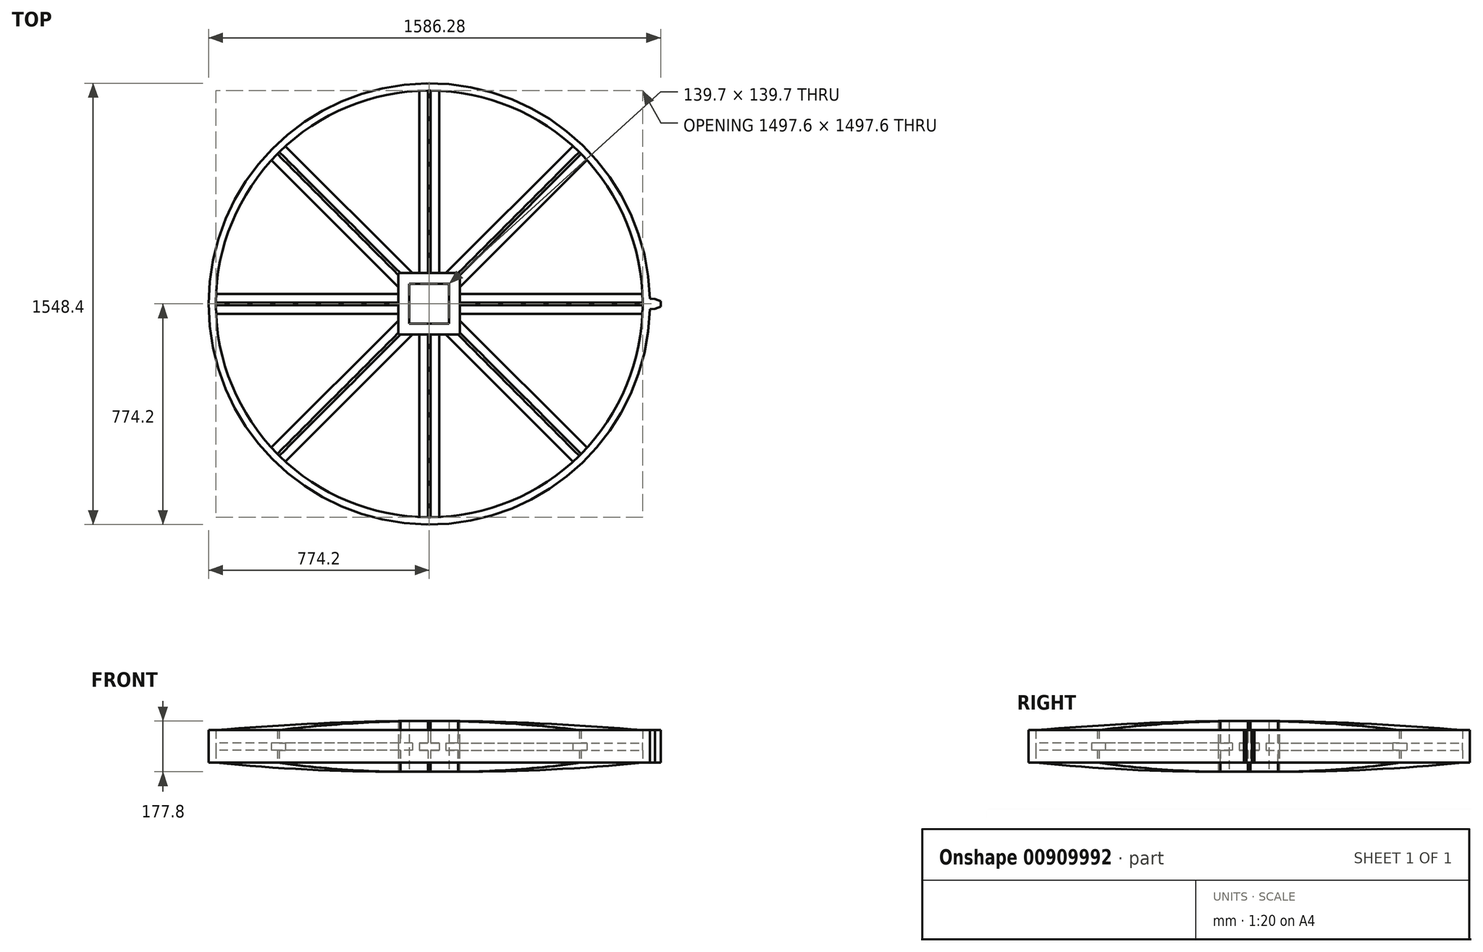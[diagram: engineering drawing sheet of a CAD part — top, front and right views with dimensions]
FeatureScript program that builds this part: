
annotation { "Feature Type Name" : "Feature", "Feature Type Description" : "" }
export const myFeature = defineFeature(function(context is Context, id is Id, definition is map)
    precondition{}
    {
        {
            var Q0;
            Q0=qCreatedBy(makeId("Front.planeOp"),FACE);
            var sketch = newSketch(context, id + "F0", { "sketchPlane" : qUnion([Q0])});
            skLineSegment(sketch, "E0.bottom", {"start": v(0, -88.9) * mm, "end": v(107.95, -88.9) * mm});
            skLineSegment(sketch, "E0.top", {"start": v(0, 88.9) * mm, "end": v(107.95, 88.9) * mm});
            skLineSegment(sketch, "E0.left", {"start": v(0, -88.9) * mm, "end": v(0, 88.9) * mm});
            skLineSegment(sketch, "E0.right", {"start": v(107.95, -88.9) * mm, "end": v(107.95, 88.9) * mm});
            skLineSegment(sketch, "E1.bottom", {"start": v(748.8, -57.15) * mm, "end": v(774.2, -57.15) * mm});
            skLineSegment(sketch, "E1.top", {"start": v(748.8, 57.15) * mm, "end": v(774.2, 57.15) * mm});
            skLineSegment(sketch, "E1.left", {"start": v(748.8, -57.15) * mm, "end": v(748.8, 57.15) * mm});
            skLineSegment(sketch, "E1.right", {"start": v(774.2, -57.15) * mm, "end": v(774.2, 57.15) * mm});
            skLineSegment(sketch, "E2", {"start": v(82.55, 88.9) * mm, "end": v(82.55, -88.9) * mm});
            skLineSegment(sketch, "E3", {"start": v(82.55, 12.5) * mm, "end": v(748.8, 12.5) * mm});
            skLineSegment(sketch, "E4", {"start": v(82.55, -12.9) * mm, "end": v(748.8, -12.9) * mm});
            skLineSegment(sketch, "E5", {"start": v(0, -88.9) * mm, "end": v(0, -224.91) * mm, "construction": true});
            skArc(sketch, "E6", {"start": v(748.8, 57.15) * mm, "mid": v(428.67, 78.96) * mm, "end": v(107.95, 88.9) * mm});
            skPoint(sketch, "E7", {"position": v(0, 0) * mm});
            skLineSegment(sketch, "E8", {"start": v(748.8, 0) * mm, "end": v(0, 0) * mm, "construction": true});
            skArc(sketch, "E9", {"start": v(107.95, -88.9) * mm, "mid": v(428.77, -80.96) * mm, "end": v(748.8, -57.15) * mm});
            skSolve(sketch);
        }
        {
            var Q0;
            {var subQ0=sQuery(id+"F0.wireOp",EDGE,"E0.left");Q0=makeQuery(id+"F0.imprint","IMPRINT",FACE,{"disambiguationData":[TD([[makeQuery(id+"F0.imprint","IMPRINT",EDGE,{"derivedFrom":subQ0}),-1.0]])]});}
            var Q1;
            {var subQ6=sQuery(id+"F0.wireOp",EDGE,"E2");Q1=makeQuery(id+"F0.imprint","IMPRINT",FACE,{"disambiguationData":[TD([[makeQuery(id+"F0.imprint","IMPRINT",EDGE,{"derivedFrom":subQ6}),1.0]])]});}
            var Q2;
            Q2=sQuery(id+"F0.wireOp",EDGE,"E0.left");
            revolve(context, id + "F1", {"surfaceOperationType" : NewSurfaceOperationType.NEW, "entities" : qUnion([Q0, Q1]), "axis" : qUnion([Q2]), "revolveType" : RevolveType.SYMMETRIC, "angle" : 45 * degree});
        }
        {
            var Q0;
            {var subQ0=sQuery(id+"F0.wireOp",EDGE,"E4");var subQ1=sQuery(id+"F0.wireOp",EDGE,"E0.right");var subQ2=makeQuery(id+"F0.imprint","INTERSECT",VERTEX,{"derivedFrom":[subQ1,subQ0]});Q0=makeQuery(id+"F0.imprint","IMPRINT",FACE,{"disambiguationData":[TD([[makeQuery(id+"F0.imprint","IMPRINT",EDGE,{"disambiguationData":[TD([[subQ2,-1.0]])],"derivedFrom":subQ1}),-1.0]])]});}
            var Q1;
            {var subQ0=sQuery(id+"F0.wireOp",EDGE,"E4");var subQ1=sQuery(id+"F0.wireOp",EDGE,"E0.right");var subQ2=makeQuery(id+"F0.imprint","INTERSECT",VERTEX,{"derivedFrom":[subQ1,subQ0]});Q1=makeQuery(id+"F0.imprint","IMPRINT",FACE,{"disambiguationData":[TD([[makeQuery(id+"F0.imprint","IMPRINT",EDGE,{"disambiguationData":[TD([[subQ2,-1.0]])],"derivedFrom":subQ1}),1.0]])]});}
            extrude(context, id + "F2", {"entities" : qUnion([Q0, Q1]), "operationType" : NewBodyOperationType.ADD, "depth" : 69.85 * mm, "offsetDistance" : 25 * mm, "symmetric" : true});
        }
        {
            var Q0;
            {var subQ3=sQuery(id+"F0.wireOp",EDGE,"E1.bottom");Q0=makeQuery(id+"F0.imprint","IMPRINT",FACE,{"disambiguationData":[TD([[makeQuery(id+"F0.imprint","IMPRINT",EDGE,{"derivedFrom":subQ3}),1.0]])]});}
            var Q1;
            Q1=sQuery(id+"F0.wireOp",EDGE,"E0.left");
            revolve(context, id + "F3", {"operationType" : NewBodyOperationType.ADD, "surfaceOperationType" : NewSurfaceOperationType.NEW, "entities" : qUnion([Q0]), "axis" : qUnion([Q1]), "revolveType" : RevolveType.SYMMETRIC, "angle" : 45 * degree});
        }
        {
            var Q0;
            {var subQ1=sQuery(id+"F0.wireOp",EDGE,"E0.top");var subQ3=sQuery(id+"F0.wireOp",EDGE,"E2");var subQ4=makeQuery(id+"F0.imprint","INTERSECT",VERTEX,{"derivedFrom":[subQ1,subQ3]});Q0=makeQuery(id+"F0.imprint","IMPRINT",FACE,{"disambiguationData":[TD([[makeQuery(id+"F0.imprint","IMPRINT",EDGE,{"disambiguationData":[TD([[subQ4,-1.0]])],"derivedFrom":subQ3}),1.0]])]});}
            var Q1;
            {var subQ1=sQuery(id+"F0.wireOp",EDGE,"E0.bottom");var subQ3=sQuery(id+"F0.wireOp",EDGE,"E2");var subQ4=makeQuery(id+"F0.imprint","INTERSECT",VERTEX,{"derivedFrom":[subQ1,subQ3]});Q1=makeQuery(id+"F0.imprint","IMPRINT",FACE,{"disambiguationData":[TD([[makeQuery(id+"F0.imprint","IMPRINT",EDGE,{"disambiguationData":[TD([[subQ4,1.0]])],"derivedFrom":subQ3}),1.0]])]});}
            var Q2;
            {var subQ0=sQuery(id+"F0.wireOp",EDGE,"E6");Q2=makeQuery(id+"F0.imprint","IMPRINT",FACE,{"disambiguationData":[TD([[makeQuery(id+"F0.imprint","IMPRINT",EDGE,{"derivedFrom":subQ0}),1.0]])]});}
            var Q3;
            {var subQ0=sQuery(id+"F0.wireOp",EDGE,"E9");Q3=makeQuery(id+"F0.imprint","IMPRINT",FACE,{"disambiguationData":[TD([[makeQuery(id+"F0.imprint","IMPRINT",EDGE,{"derivedFrom":subQ0}),1.0]])]});}
            extrude(context, id + "F4", {"entities" : qUnion([Q0, Q1, Q2, Q3]), "operationType" : NewBodyOperationType.ADD, "depth" : 9.53 * mm, "offsetDistance" : 25 * mm, "symmetric" : true});
        }
        {
            var Q0;
            Q0=makeQuery(id+"F1.opRevolve","SWEPT_BODY",BODY,{"disambiguationData":[OSD([sQuery(id+"F0.wireOp",EDGE,"E0.bottom"),sQuery(id+"F0.wireOp",EDGE,"E0.top"),sQuery(id+"F0.wireOp",EDGE,"E0.left"),sQuery(id+"F0.wireOp",EDGE,"E0.right")])]});
            var Q1;
            Q1=sQuery(id+"F0.wireOp",EDGE,"E0.left");
            circularPattern(context, id + "F5", {"operationType" : NewBodyOperationType.ADD, "entities" : qUnion([Q0]), "axis" : qUnion([Q1]), "angle" : 360 * degree, "instanceCount" : 8, "equalSpace" : true});
        }
        {
            var Q0;
            {var subQ0=makeQuery(id+"F3.opRevolve","SWEPT_FACE",FACE,{"disambiguationData":[OSD([sQuery(id+"F0.wireOp",EDGE,"E1.top")])]});Q0=makeQuery(id+"F5.boolean.opBoolean","MERGE",FACE,{"derivedFrom":[subQ0,makeQuery(id+"F5.opPattern","COPY",FACE,{"derivedFrom":subQ0,"instanceName":"1"}),makeQuery(id+"F5.opPattern","COPY",FACE,{"derivedFrom":subQ0,"instanceName":"2"}),makeQuery(id+"F5.opPattern","COPY",FACE,{"derivedFrom":subQ0,"instanceName":"3"}),makeQuery(id+"F5.opPattern","COPY",FACE,{"derivedFrom":subQ0,"instanceName":"4"}),makeQuery(id+"F5.opPattern","COPY",FACE,{"derivedFrom":subQ0,"instanceName":"5"}),makeQuery(id+"F5.opPattern","COPY",FACE,{"derivedFrom":subQ0,"instanceName":"6"}),makeQuery(id+"F5.opPattern","COPY",FACE,{"derivedFrom":subQ0,"instanceName":"7"})]});}
            var sketch = newSketch(context, id + "F6", { "sketchPlane" : qUnion([Q0])});
            skLineSegment(sketch, "E10", {"start": v(773.98, 18.26) * mm, "end": v(792.56, 16.63) * mm});
            skLineSegment(sketch, "E11", {"start": v(792.56, 16.63) * mm, "end": v(812.08, 9.53) * mm});
            skLineSegment(sketch, "E12", {"start": v(812.08, 9.53) * mm, "end": v(812.08, -9.53) * mm});
            skLineSegment(sketch, "E13", {"start": v(812.08, -9.53) * mm, "end": v(792.56, -16.63) * mm});
            skLineSegment(sketch, "E14", {"start": v(792.56, -16.63) * mm, "end": v(773.98, -18.26) * mm});
            skLineSegment(sketch, "E15", {"start": v(0, 0) * mm, "end": v(812.08, 0) * mm, "construction": true});
            skLineSegment(sketch, "E16", {"start": v(773.98, 18.26) * mm, "end": v(773.98, -18.26) * mm});
            skSolve(sketch);
        }
        {
            var Q0;
            {var subQ0=sQuery(id+"F6.wireOp",EDGE,"E10");Q0=makeQuery(id+"F6.imprint","IMPRINT",FACE,{"disambiguationData":[TD([[makeQuery(id+"F6.imprint","IMPRINT",EDGE,{"derivedFrom":subQ0}),-1.0]])]});}
            var Q1;
            {var subQ0=sQuery(id+"F0.wireOp",EDGE,"E0.bottom");var subQ1=makeQuery(id+"F4.boolean.opBoolean","MERGE",FACE,{"derivedFrom":[makeQuery(id+"F1.opRevolve","SWEPT_FACE",FACE,{"disambiguationData":[OSD([subQ0])]}),makeQuery(id+"F3.opRevolve","SWEPT_FACE",FACE,{"disambiguationData":[OSD([sQuery(id+"F0.wireOp",EDGE,"E1.bottom")])]}),makeQuery(id+"F4.opExtrude","SWEPT_FACE",FACE,{"disambiguationData":[OSD([subQ0,sQuery(id+"F0.wireOp",EDGE,"D5k9asr0-8ta1-f4uu-XxQ3-tXAVFih4KlHv")])]})]});Q1=makeQuery(id+"F5.boolean.opBoolean","MERGE",FACE,{"derivedFrom":[subQ1,makeQuery(id+"F5.opPattern","COPY",FACE,{"derivedFrom":subQ1,"instanceName":"1"}),makeQuery(id+"F5.opPattern","COPY",FACE,{"derivedFrom":subQ1,"instanceName":"2"}),makeQuery(id+"F5.opPattern","COPY",FACE,{"derivedFrom":subQ1,"instanceName":"3"}),makeQuery(id+"F5.opPattern","COPY",FACE,{"derivedFrom":subQ1,"instanceName":"4"}),makeQuery(id+"F5.opPattern","COPY",FACE,{"derivedFrom":subQ1,"instanceName":"5"}),makeQuery(id+"F5.opPattern","COPY",FACE,{"derivedFrom":subQ1,"instanceName":"6"}),makeQuery(id+"F5.opPattern","COPY",FACE,{"derivedFrom":subQ1,"instanceName":"7"})]});}
            extrude(context, id + "F7", {"entities" : qUnion([Q0]), "operationType" : NewBodyOperationType.ADD, "oppositeDirection" : true, "depth" : 114.3 * mm, "endBoundEntityFace" : qUnion([Q1]), "offsetDistance" : 25 * mm});
        }
        {
            var Q0;
            {var subQ0=sQuery(id+"F0.wireOp",EDGE,"E0.bottom");var subQ1=makeQuery(id+"F4.boolean.opBoolean","MERGE",FACE,{"derivedFrom":[makeQuery(id+"F1.opRevolve","SWEPT_FACE",FACE,{"disambiguationData":[OSD([subQ0])]}),makeQuery(id+"F3.opRevolve","SWEPT_FACE",FACE,{"disambiguationData":[OSD([sQuery(id+"F0.wireOp",EDGE,"E1.bottom")])]}),makeQuery(id+"F4.opExtrude","SWEPT_FACE",FACE,{"disambiguationData":[OSD([subQ0,sQuery(id+"F0.wireOp",EDGE,"D5k9asr0-8ta1-f4uu-XxQ3-tXAVFih4KlHv")])]})]});Q0=makeQuery(id+"F5.boolean.opBoolean","MERGE",FACE,{"derivedFrom":[subQ1,makeQuery(id+"F5.opPattern","COPY",FACE,{"derivedFrom":subQ1,"instanceName":"1"}),makeQuery(id+"F5.opPattern","COPY",FACE,{"derivedFrom":subQ1,"instanceName":"2"}),makeQuery(id+"F5.opPattern","COPY",FACE,{"derivedFrom":subQ1,"instanceName":"3"}),makeQuery(id+"F5.opPattern","COPY",FACE,{"derivedFrom":subQ1,"instanceName":"4"}),makeQuery(id+"F5.opPattern","COPY",FACE,{"derivedFrom":subQ1,"instanceName":"5"}),makeQuery(id+"F5.opPattern","COPY",FACE,{"derivedFrom":subQ1,"instanceName":"6"}),makeQuery(id+"F5.opPattern","COPY",FACE,{"derivedFrom":subQ1,"instanceName":"7"})]});}
            var sketch = newSketch(context, id + "F8", { "sketchPlane" : qUnion([Q0])});
            skLineSegment(sketch, "E17.bottom", {"start": v(-69.85, 69.85) * mm, "end": v(69.85, 69.85) * mm});
            skLineSegment(sketch, "E17.top", {"start": v(-69.85, -69.85) * mm, "end": v(69.85, -69.85) * mm});
            skLineSegment(sketch, "E17.left", {"start": v(-69.85, 69.85) * mm, "end": v(-69.85, -69.85) * mm});
            skLineSegment(sketch, "E17.right", {"start": v(69.85, 69.85) * mm, "end": v(69.85, -69.85) * mm});
            skLineSegment(sketch, "E18", {"start": v(-69.85, 69.85) * mm, "end": v(69.85, -69.85) * mm, "construction": true});
            skLineSegment(sketch, "E19", {"start": v(69.85, 69.85) * mm, "end": v(-69.85, -69.85) * mm, "construction": true});
            skLineSegment(sketch, "E20.bottom", {"start": v(-107.95, -107.95) * mm, "end": v(107.95, -107.95) * mm});
            skLineSegment(sketch, "E20.top", {"start": v(-107.95, 107.95) * mm, "end": v(107.95, 107.95) * mm});
            skLineSegment(sketch, "E20.left", {"start": v(-107.95, -107.95) * mm, "end": v(-107.95, 107.95) * mm});
            skLineSegment(sketch, "E20.right", {"start": v(107.95, -107.95) * mm, "end": v(107.95, 107.95) * mm});
            skSolve(sketch);
        }
        {
            var Q0;
            {var subQ2=sQuery(id+"F0.wireOp",EDGE,"E0.bottom");var subQ3=makeQuery(id+"F4.opExtrude","CAP_EDGE",EDGE,{"disambiguationData":[OSD([subQ2])],"isStart":true});var subQ4=makeQuery(id+"F5.opPattern","COPY",EDGE,{"derivedFrom":subQ3,"instanceName":"2"});Q0=makeQuery(id+"F8.imprint","IMPRINT",FACE,{"disambiguationData":[TD([[makeQuery(id+"F8.imprint","IMPRINT",EDGE,{"derivedFrom":subQ4}),-1.0]])]});}
            var Q1;
            {var subQ2=sQuery(id+"F0.wireOp",EDGE,"E0.bottom");var subQ3=makeQuery(id+"F4.opExtrude","CAP_EDGE",EDGE,{"disambiguationData":[OSD([subQ2])],"isStart":true});var subQ4=makeQuery(id+"F5.opPattern","COPY",EDGE,{"derivedFrom":subQ3,"instanceName":"4"});Q1=makeQuery(id+"F8.imprint","IMPRINT",FACE,{"disambiguationData":[TD([[makeQuery(id+"F8.imprint","IMPRINT",EDGE,{"derivedFrom":subQ4}),-1.0]])]});}
            var Q2;
            {var subQ0=sQuery(id+"F0.wireOp",EDGE,"E0.bottom");var subQ3=makeQuery(id+"F4.opExtrude","CAP_EDGE",EDGE,{"disambiguationData":[OSD([subQ0])],"isStart":false});Q2=makeQuery(id+"F8.imprint","IMPRINT",FACE,{"disambiguationData":[TD([[makeQuery(id+"F8.imprint","IMPRINT",EDGE,{"derivedFrom":subQ3}),1.0]])]});}
            var Q3;
            {var subQ2=sQuery(id+"F0.wireOp",EDGE,"E0.bottom");var subQ4=makeQuery(id+"F4.opExtrude","CAP_EDGE",EDGE,{"disambiguationData":[OSD([subQ2])],"isStart":true});Q3=makeQuery(id+"F8.imprint","IMPRINT",FACE,{"disambiguationData":[TD([[makeQuery(id+"F8.imprint","IMPRINT",EDGE,{"derivedFrom":subQ4}),-1.0]])]});}
            var Q4;
            Q4=makeQuery(id+"F8.imprint","IMPRINT",FACE,{"disambiguationData":[TD([[makeQuery(id+"F8.imprint","IMPRINT",EDGE,{"derivedFrom":sQuery(id+"F8.wireOp",EDGE,"E17.bottom")}),1.0]])]});
            extrude(context, id + "F9", {"entities" : qUnion([Q0, Q1, Q2, Q3, Q4]), "operationType" : NewBodyOperationType.ADD, "oppositeDirection" : true, "depth" : 177.8 * mm, "offsetDistance" : 25 * mm});
        }
        {
            var Q0;
            Q0=makeQuery(id+"F8.imprint","IMPRINT",FACE,{"disambiguationData":[TD([[makeQuery(id+"F8.imprint","IMPRINT",EDGE,{"derivedFrom":sQuery(id+"F8.wireOp",EDGE,"E17.bottom")}),-1.0]])]});
            extrude(context, id + "F10", {"entities" : qUnion([Q0]), "operationType" : NewBodyOperationType.REMOVE, "endBound" : BoundingType.THROUGH_ALL, "oppositeDirection" : true, "depth" : 25 * mm, "offsetDistance" : 25 * mm});
        }
    });
